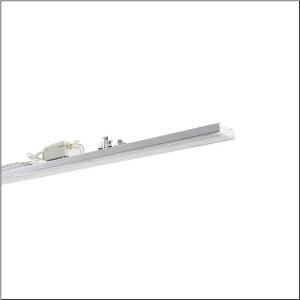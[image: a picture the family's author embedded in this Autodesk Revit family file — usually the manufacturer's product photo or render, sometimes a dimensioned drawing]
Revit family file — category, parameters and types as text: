
# Revit family: licross_r__11_recessed_extreme_mo_51te12dv4fxge_8f4a
name_source: partatom
category: Lighting Fixtures
units: mm (PartAtom-declared; Revit-internal decimal feet)

## family parameters
Cut with Voids When Loaded = No
Host = Face
Light Source = No
Part Type = Normal
Room Calculation Point = No
Round Connector Dimension = Use Diameter
Shared = No

## types (1)
- --- (1 x LED, 15360 lm, 84.1 W, 4000K)
    Apparent Load = 84 VA
    CIE Flux Codes = 67 92 99 100 100
    Color Rendering = 80
    Color Temperature = 4000K
    Default Elevation = 1800 mm
    Description = Licross® 11 Recessed extreme MO, luminaire insert, of sheet steel, galvanised, coil coated, white, length: 2.250mm, width: 66mm, height: 67mm, LED rated luminous flux: 15.360lm, light colour: 840, control gear: DALI 2, with plug, 5-pole, with phase selection, mains connection: 220..240V, AC, 50/60Hz, rated input power: 84W, halogen-free wiring, primary optical cover: cover, of PMMA, light emission: direct distribution, primary light characteristic: symmetric, protection rating (complete): IP54, insulation class (complete): insulation class I (protective earthing), certification: CE, ENEC, VDE, UKCA, protection symbol: D if used in an environment with non-conductive dust loads with corresponding accessories, impact resistance: IK06, permissible ambient temperature for indoor applications: -40..+45°C, corresponds to IFS (International Featured Standards) requirements for safety and quality in the food industry, reducing of maximum allowable ambient temperature of 5°C with ceiling mounting, LABS conformity tested according to VDMA 24364:2018-05, packaging unit: 1 piece
    Height = 58 mm
    Lamp = 1 x LED
    Lamp Light Flux = 15360 lm
    Lamp Power = 84.1 W
    Lamp count = 1
    Length = 2250 mm
    Luminous efficacy = 183 lm/W
    Manufacturer = Siteco
    ModVariant = No
    Model = 51TE12DV4FXGE
    Mounting Place = Ceiling
    Mounting Type = Pendant
    Number of Poles = 1
    OnlyDefault = Yes
    Power Factor = 1
    Product Name = Licross® 11 Recessed extreme MO
    Product group = luminaire insert
    ProductGroupID = 901
    Protection Class = Protection class I
    Protection Degree = IP 54
    RLX_Detail_Level = 1
    RLX_Emergency_Light_Flux = 0 lm
    RLX_Emergency_Type = 0
    RLX_Emergency_Type_DB = No
    RlxData = <blob elided: 29429 chars, md5=5e0234c0>
    Socket = socket
    Standby Power = 0 W
    System Light Flux = 15360 lm
    System Power = 84 W
    Type Comments = factory setting: luminous flux: 100 % | dim-lin: 254 | 378 mA
    Type Image = l_1296930.jpg
    URL = http://relux.com
    VarID = @adj_077572
    Voltage = 0 V
    Weight = 0.00 kg
    Width = 66 mm

## geometry (parser evidence)
native form markers: Blend x4, Sweep x11
no freeform markers — native parametric forms only
